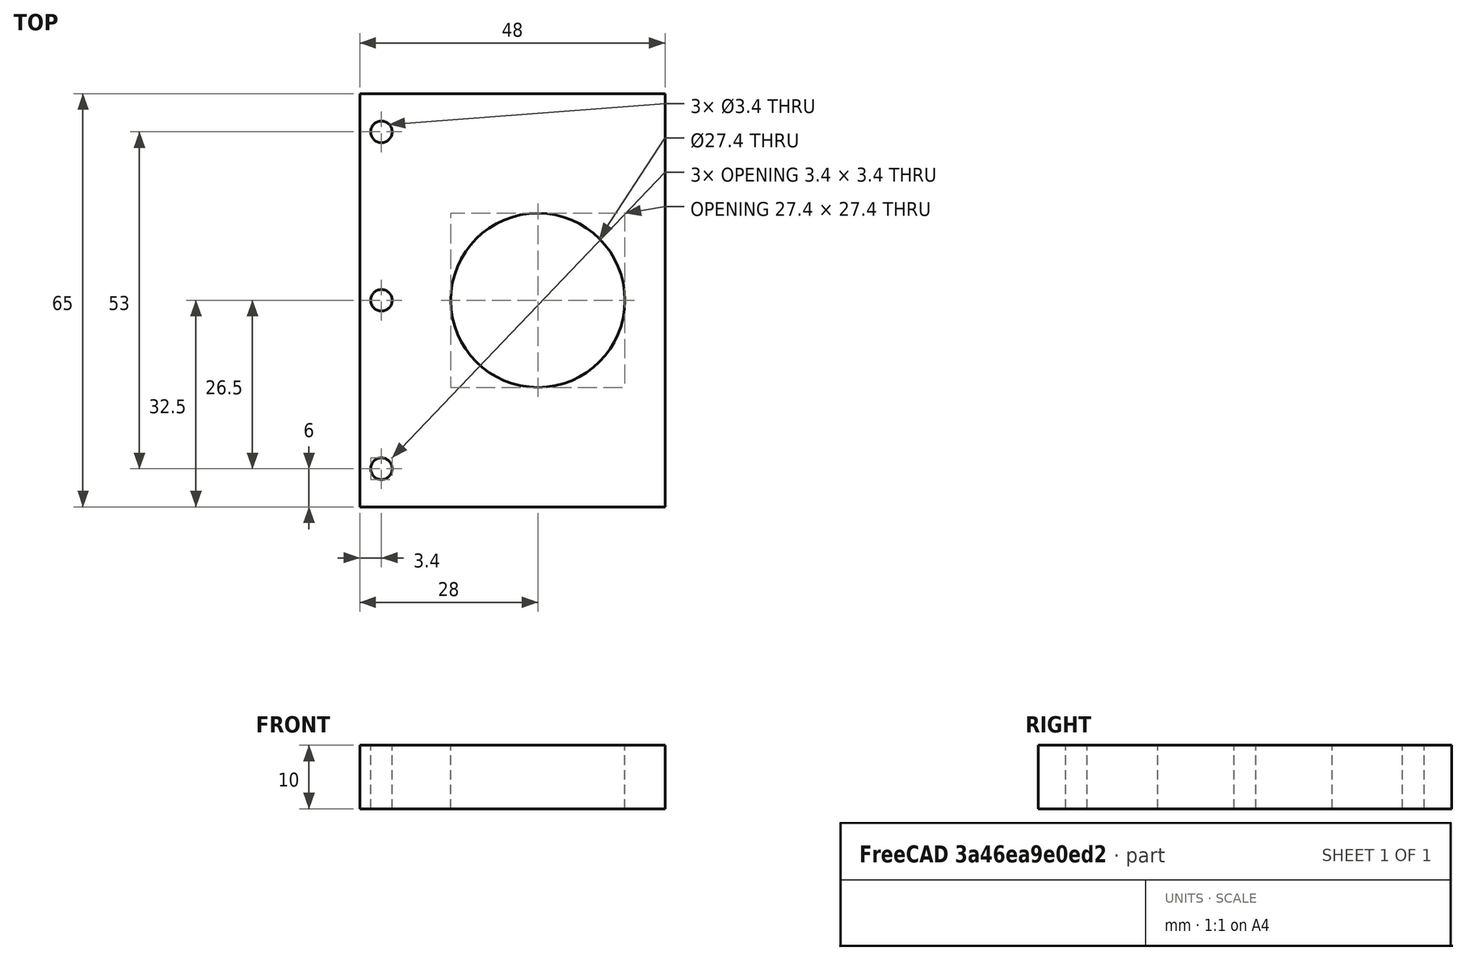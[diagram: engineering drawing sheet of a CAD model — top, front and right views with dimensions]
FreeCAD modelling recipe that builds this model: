
FCSTD DOCUMENT
Label: camera_mount_minimal
objects: Part::Cylinder×4, Part::Cut×4, Part::Box×1
note: 9 computed .brp shape members not serialized (recipe doc carries the construction recipe); baked Part::Feature solids carry a one-line shape summary decoded from their .brp

FEATURE [Part::Cylinder] Cylinder
  Angle = 360
  Height = 50
  Placement = pos=(28,32.5,-5) rot=(0,0,1;0rad)
  Radius = 13.7
FEATURE [Part::Cylinder] Cylinder002
  Angle = 360
  Height = 20
  Placement = pos=(3.4,32.5,-5) rot=(0,0,1;0rad)
  Radius = 1.7
FEATURE [Part::Cylinder] Cylinder003
  Angle = 360
  Height = 20
  Placement = pos=(3.4,59,-5) rot=(0,0,1;0rad)
  Radius = 1.7
FEATURE [Part::Box] Box
  Height = 10
  Length = 48
  Width = 65
FEATURE [Part::Cylinder] Cylinder005
  Angle = 360
  Height = 20
  Placement = pos=(3.4,6,-5) rot=(0,0,1;0rad)
  Radius = 1.7
FEATURE [Part::Cut] Cut
  Base = -> Box
  Tool = -> Cylinder
FEATURE [Part::Cut] Cut001
  Base = -> Cut
  Tool = -> Cylinder002
FEATURE [Part::Cut] Cut002
  Base = -> Cut001
  Tool = -> Cylinder005
FEATURE [Part::Cut] Cut003
  Base = -> Cut002
  Tool = -> Cylinder003
